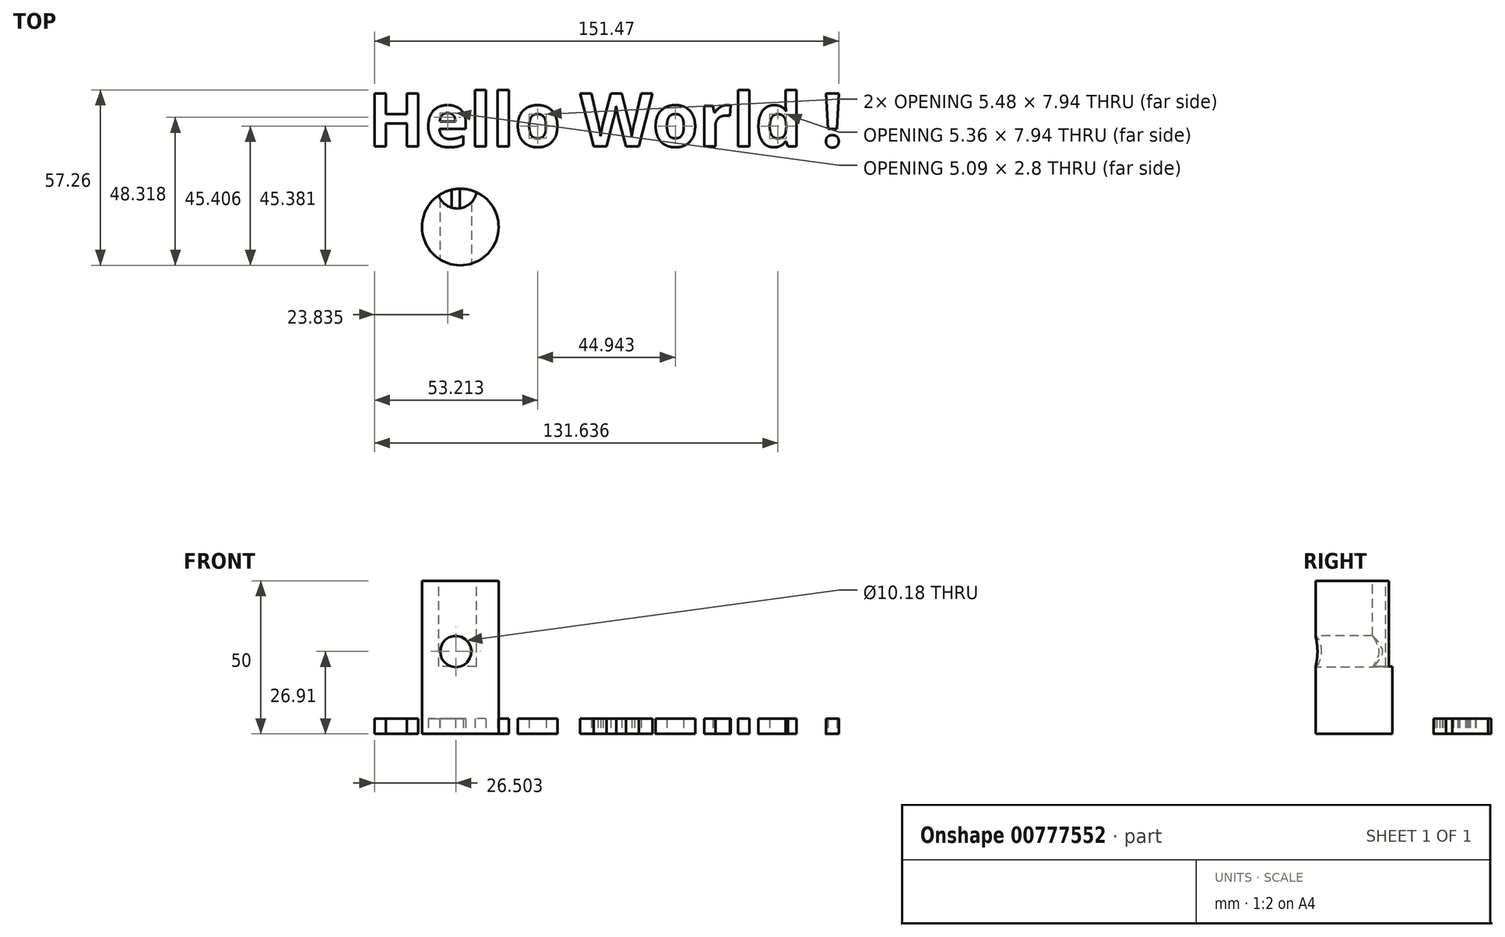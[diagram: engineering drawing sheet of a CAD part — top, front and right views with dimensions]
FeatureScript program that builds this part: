
annotation { "Feature Type Name" : "Feature", "Feature Type Description" : "" }
export const myFeature = defineFeature(function(context is Context, id is Id, definition is map)
    precondition{}
    {
        {
            var Q0;
            Q0=qCreatedBy(makeId("Top.planeOp"),FACE);
            var sketch = newSketch(context, id + "F0", { "sketchPlane" : qUnion([Q0])});
            skCircle(sketch, "E0", {"center": v(-22.37, 20.1) * mm, "radius": 12.5 * mm});
            skSolve(sketch);
        }
        {
            var Q0;
            Q0 = qSketchRegion(id + "F0", true);
            extrude(context, id + "F1", {"entities" : qUnion([Q0]), "depth" : 50 * mm, "offsetDistance" : 25 * mm});
        }
        {
            var Q0;
            Q0=qCreatedBy(makeId("Front.planeOp"),FACE);
            var sketch = newSketch(context, id + "F2", { "sketchPlane" : qUnion([Q0])});
            skCircle(sketch, "E1", {"center": v(-23.86, 26.9) * mm, "radius": 5.1 * mm});
            skSolve(sketch);
        }
        {
            var Q0;
            Q0 = qSketchRegion(id + "F2", true);
            extrude(context, id + "F3", {"entities" : qUnion([Q0]), "operationType" : NewBodyOperationType.REMOVE, "oppositeDirection" : true, "depth" : 35 * mm, "offsetDistance" : 25 * mm});
        }
        {
            var Q0;
            Q0=makeQuery(id+"F1.opExtrude","CAP_FACE",FACE,{"disambiguationData":[OSD([sQuery(id+"F0.wireOp",EDGE,"E0")])],"isStart":false});
            var sketch = newSketch(context, id + "F4", { "sketchPlane" : qUnion([Q0])});
            skCircle(sketch, "E2", {"center": v(-23.39, 32.56) * mm, "radius": 6.4 * mm});
            skSolve(sketch);
        }
        {
            var Q0;
            Q0 = qSketchRegion(id + "F4", true);
            extrude(context, id + "F5", {"entities" : qUnion([Q0]), "operationType" : NewBodyOperationType.REMOVE, "oppositeDirection" : true, "depth" : 28 * mm, "offsetDistance" : 25 * mm});
        }
        {
            var Q0;
            Q0=qCreatedBy(makeId("Top.planeOp"),FACE);
            var sketch = newSketch(context, id + "F6", { "sketchPlane" : qUnion([Q0])});
            skText(sketch, "E3", { "text": "Hello World !", "fontName": "OpenSans-Bold.ttf"});
            const initialGuessF6  = {"E3": [-0.05255, 0.04636, 1, 0, 0.01753]};
            skSetInitialGuess(sketch, initialGuessF6);
            skSolve(sketch);
        }
        {
            var Q0;
            Q0 = qSketchRegion(id + "F6", true);
            extrude(context, id + "F7", {"entities" : qUnion([Q0]), "depth" : 5 * mm, "offsetDistance" : 25 * mm});
        }
    });
